annotation { "Feature Type Name" : "Feature", "Feature Type Description" : "" }
export const myFeature = defineFeature(function(context is Context, id is Id, definition is map)
    precondition{}
    {
        {
            var Q0;
            Q0=qCreatedBy(makeId("Front.planeOp"),FACE);
            var sketch = newSketch(context, id + "F0", { "sketchPlane" : qUnion([Q0])});
            skLineSegment(sketch, "E0", {"start": v(-75.47, 38.87) * mm, "end": v(-75.47, -34.46) * mm});
            skLineSegment(sketch, "E1.MirrorCS", {"start": v(75.47, 38.87) * mm, "end": v(75.47, -34.46) * mm});
            skLineSegment(sketch, "E2", {"start": v(-75.47, -34.46) * mm, "end": v(75.47, -34.46) * mm});
            skLineSegment(sketch, "E3", {"start": v(-75.47, 38.87) * mm, "end": v(75.47, 38.87) * mm});
            skText(sketch, "E4", { "text": "Rap Monster", "fontName": "OpenSans-Regular.ttf"});
            skText(sketch, "E5", { "text": "94", "fontName": "OpenSans-Regular.ttf"});
            const initialGuessF0  = {"E4": [-0.03494, 0.0229, 1, 0, 0.00846], "E5": [-0.03435, -0.02477, 1, 0, 0.04185]};
            skSetInitialGuess(sketch, initialGuessF0);
            skSolve(sketch);
        }
        {
            var Q0;
            Q0=makeQuery(id+"F0.imprint","IMPRINT",FACE,{"disambiguationData":[TD([[makeQuery(id+"F0.imprint","IMPRINT",EDGE,{"derivedFrom":sQuery(id+"F0.wireOp",EDGE,"E0")}),1.0]])]});
            extrude(context, id + "F1", {"entities" : qUnion([Q0]), "depth" : 3 * mm, "offsetDistance" : 25.4 * mm});
        }
        {
            var Q0;
            Q0=qCreatedBy(makeId("Front.planeOp"),FACE);
            var sketch = newSketch(context, id + "F2", { "sketchPlane" : qUnion([Q0])});
            skLineSegment(sketch, "E6.bottom", {"start": v(75.47, 38.9) * mm, "end": v(-75.55, 38.9) * mm});
            skLineSegment(sketch, "E6.top", {"start": v(75.47, -34.58) * mm, "end": v(-75.55, -34.58) * mm});
            skLineSegment(sketch, "E6.left", {"start": v(75.47, 38.9) * mm, "end": v(75.47, -34.58) * mm});
            skLineSegment(sketch, "E6.right", {"start": v(-75.55, 38.9) * mm, "end": v(-75.55, -34.58) * mm});
            skSolve(sketch);
        }
        {
            var Q0;
            Q0 = qSketchRegion(id + "F2", true);
            extrude(context, id + "F3", {"entities" : qUnion([Q0]), "operationType" : NewBodyOperationType.ADD, "oppositeDirection" : true, "depth" : 3 * mm, "offsetDistance" : 25.4 * mm});
        }
        {
            var Q0;
            Q0=makeQuery(id+"F0.imprint","IMPRINT",FACE,{"disambiguationData":[TD([[makeQuery(id+"F0.imprint","IMPRINT",EDGE,{"derivedFrom":sQuery(id+"F0.wireOp",EDGE,"E5.sketch_text.stroke-37")}),1.0]])]});
            var Q1;
            Q1=makeQuery(id+"F0.imprint","IMPRINT",FACE,{"disambiguationData":[TD([[makeQuery(id+"F0.imprint","IMPRINT",EDGE,{"derivedFrom":sQuery(id+"F0.wireOp",EDGE,"E5.sketch_text.stroke-16")}),1.0]])]});
            var Q2;
            Q2=makeQuery(id+"F0.imprint","IMPRINT",FACE,{"disambiguationData":[TD([[makeQuery(id+"F0.imprint","IMPRINT",EDGE,{"derivedFrom":sQuery(id+"F0.wireOp",EDGE,"E4.sketch_text.stroke-37")}),1.0]])]});
            var Q3;
            Q3=makeQuery(id+"F0.imprint","IMPRINT",FACE,{"disambiguationData":[TD([[makeQuery(id+"F0.imprint","IMPRINT",EDGE,{"derivedFrom":sQuery(id+"F0.wireOp",EDGE,"E4.sketch_text.stroke-11")}),1.0]])]});
            var Q4;
            Q4=makeQuery(id+"F0.imprint","IMPRINT",FACE,{"disambiguationData":[TD([[makeQuery(id+"F0.imprint","IMPRINT",EDGE,{"derivedFrom":sQuery(id+"F0.wireOp",EDGE,"E4.sketch_text.stroke-61")}),1.0]])]});
            var Q5;
            Q5=makeQuery(id+"F0.imprint","IMPRINT",FACE,{"disambiguationData":[TD([[makeQuery(id+"F0.imprint","IMPRINT",EDGE,{"derivedFrom":sQuery(id+"F0.wireOp",EDGE,"E4.sketch_text.stroke-97")}),1.0]])]});
            var Q6;
            Q6=makeQuery(id+"F0.imprint","IMPRINT",FACE,{"disambiguationData":[TD([[makeQuery(id+"F0.imprint","IMPRINT",EDGE,{"derivedFrom":sQuery(id+"F0.wireOp",EDGE,"E4.sketch_text.stroke-180")}),1.0]])]});
            extrude(context, id + "F4", {"entities" : qUnion([Q0, Q1, Q2, Q3, Q4, Q5, Q6]), "operationType" : NewBodyOperationType.ADD, "depth" : 3 * mm, "offsetDistance" : 25.4 * mm});
        }
        {
            var Q0;
            Q0=makeQuery(id+"F1.opExtrude","CAP_FACE",FACE,{"disambiguationData":[OSD([sQuery(id+"F0.wireOp",EDGE,"E0"),sQuery(id+"F0.wireOp",EDGE,"E1.MirrorCS"),sQuery(id+"F0.wireOp",EDGE,"E2"),sQuery(id+"F0.wireOp",EDGE,"E3"),sQuery(id+"F0.wireOp",EDGE,"E4.sketch_text.stroke-0"),sQuery(id+"F0.wireOp",EDGE,"E4.sketch_text.stroke-1"),sQuery(id+"F0.wireOp",EDGE,"E4.sketch_text.stroke-2"),sQuery(id+"F0.wireOp",EDGE,"E4.sketch_text.stroke-3"),sQuery(id+"F0.wireOp",EDGE,"E4.sketch_text.stroke-4"),sQuery(id+"F0.wireOp",EDGE,"E4.sketch_text.stroke-5"),sQuery(id+"F0.wireOp",EDGE,"E4.sketch_text.stroke-6"),sQuery(id+"F0.wireOp",EDGE,"E4.sketch_text.stroke-7"),sQuery(id+"F0.wireOp",EDGE,"E4.sketch_text.stroke-8"),sQuery(id+"F0.wireOp",EDGE,"E4.sketch_text.stroke-9"),sQuery(id+"F0.wireOp",EDGE,"E4.sketch_text.stroke-10"),sQuery(id+"F0.wireOp",EDGE,"E4.sketch_text.stroke-18"),sQuery(id+"F0.wireOp",EDGE,"E4.sketch_text.stroke-19"),sQuery(id+"F0.wireOp",EDGE,"E4.sketch_text.stroke-20"),sQuery(id+"F0.wireOp",EDGE,"E4.sketch_text.stroke-21"),sQuery(id+"F0.wireOp",EDGE,"E4.sketch_text.stroke-22"),sQuery(id+"F0.wireOp",EDGE,"E4.sketch_text.stroke-23"),sQuery(id+"F0.wireOp",EDGE,"E4.sketch_text.stroke-24"),sQuery(id+"F0.wireOp",EDGE,"E4.sketch_text.stroke-25"),sQuery(id+"F0.wireOp",EDGE,"E4.sketch_text.stroke-26"),sQuery(id+"F0.wireOp",EDGE,"E4.sketch_text.stroke-27"),sQuery(id+"F0.wireOp",EDGE,"E4.sketch_text.stroke-28"),sQuery(id+"F0.wireOp",EDGE,"E4.sketch_text.stroke-29"),sQuery(id+"F0.wireOp",EDGE,"E4.sketch_text.stroke-30"),sQuery(id+"F0.wireOp",EDGE,"E4.sketch_text.stroke-31"),sQuery(id+"F0.wireOp",EDGE,"E4.sketch_text.stroke-32"),sQuery(id+"F0.wireOp",EDGE,"E4.sketch_text.stroke-33"),sQuery(id+"F0.wireOp",EDGE,"E4.sketch_text.stroke-34"),sQuery(id+"F0.wireOp",EDGE,"E4.sketch_text.stroke-35"),sQuery(id+"F0.wireOp",EDGE,"E4.sketch_text.stroke-36"),sQuery(id+"F0.wireOp",EDGE,"E4.sketch_text.stroke-45"),sQuery(id+"F0.wireOp",EDGE,"E4.sketch_text.stroke-46"),sQuery(id+"F0.wireOp",EDGE,"E4.sketch_text.stroke-47"),sQuery(id+"F0.wireOp",EDGE,"E4.sketch_text.stroke-48"),sQuery(id+"F0.wireOp",EDGE,"E4.sketch_text.stroke-49"),sQuery(id+"F0.wireOp",EDGE,"E4.sketch_text.stroke-50"),sQuery(id+"F0.wireOp",EDGE,"E4.sketch_text.stroke-51"),sQuery(id+"F0.wireOp",EDGE,"E4.sketch_text.stroke-52"),sQuery(id+"F0.wireOp",EDGE,"E4.sketch_text.stroke-53"),sQuery(id+"F0.wireOp",EDGE,"E4.sketch_text.stroke-54"),sQuery(id+"F0.wireOp",EDGE,"E4.sketch_text.stroke-55"),sQuery(id+"F0.wireOp",EDGE,"E4.sketch_text.stroke-56"),sQuery(id+"F0.wireOp",EDGE,"E4.sketch_text.stroke-57"),sQuery(id+"F0.wireOp",EDGE,"E4.sketch_text.stroke-58"),sQuery(id+"F0.wireOp",EDGE,"E4.sketch_text.stroke-59"),sQuery(id+"F0.wireOp",EDGE,"E4.sketch_text.stroke-60"),sQuery(id+"F0.wireOp",EDGE,"E4.sketch_text.stroke-70"),sQuery(id+"F0.wireOp",EDGE,"E4.sketch_text.stroke-71"),sQuery(id+"F0.wireOp",EDGE,"E4.sketch_text.stroke-72"),sQuery(id+"F0.wireOp",EDGE,"E4.sketch_text.stroke-73"),sQuery(id+"F0.wireOp",EDGE,"E4.sketch_text.stroke-74"),sQuery(id+"F0.wireOp",EDGE,"E4.sketch_text.stroke-75"),sQuery(id+"F0.wireOp",EDGE,"E4.sketch_text.stroke-76"),sQuery(id+"F0.wireOp",EDGE,"E4.sketch_text.stroke-77"),sQuery(id+"F0.wireOp",EDGE,"E4.sketch_text.stroke-78"),sQuery(id+"F0.wireOp",EDGE,"E4.sketch_text.stroke-79"),sQuery(id+"F0.wireOp",EDGE,"E4.sketch_text.stroke-80"),sQuery(id+"F0.wireOp",EDGE,"E4.sketch_text.stroke-81"),sQuery(id+"F0.wireOp",EDGE,"E4.sketch_text.stroke-82"),sQuery(id+"F0.wireOp",EDGE,"E4.sketch_text.stroke-83"),sQuery(id+"F0.wireOp",EDGE,"E4.sketch_text.stroke-84"),sQuery(id+"F0.wireOp",EDGE,"E4.sketch_text.stroke-85"),sQuery(id+"F0.wireOp",EDGE,"E4.sketch_text.stroke-86"),sQuery(id+"F0.wireOp",EDGE,"E4.sketch_text.stroke-87"),sQuery(id+"F0.wireOp",EDGE,"E4.sketch_text.stroke-88"),sQuery(id+"F0.wireOp",EDGE,"E4.sketch_text.stroke-89"),sQuery(id+"F0.wireOp",EDGE,"E4.sketch_text.stroke-90"),sQuery(id+"F0.wireOp",EDGE,"E4.sketch_text.stroke-91"),sQuery(id+"F0.wireOp",EDGE,"E4.sketch_text.stroke-92"),sQuery(id+"F0.wireOp",EDGE,"E4.sketch_text.stroke-93"),sQuery(id+"F0.wireOp",EDGE,"E4.sketch_text.stroke-94"),sQuery(id+"F0.wireOp",EDGE,"E4.sketch_text.stroke-95"),sQuery(id+"F0.wireOp",EDGE,"E4.sketch_text.stroke-96"),sQuery(id+"F0.wireOp",EDGE,"E4.sketch_text.stroke-105"),sQuery(id+"F0.wireOp",EDGE,"E4.sketch_text.stroke-106"),sQuery(id+"F0.wireOp",EDGE,"E4.sketch_text.stroke-107"),sQuery(id+"F0.wireOp",EDGE,"E4.sketch_text.stroke-108"),sQuery(id+"F0.wireOp",EDGE,"E4.sketch_text.stroke-109"),sQuery(id+"F0.wireOp",EDGE,"E4.sketch_text.stroke-110"),sQuery(id+"F0.wireOp",EDGE,"E4.sketch_text.stroke-111"),sQuery(id+"F0.wireOp",EDGE,"E4.sketch_text.stroke-112"),sQuery(id+"F0.wireOp",EDGE,"E4.sketch_text.stroke-113"),sQuery(id+"F0.wireOp",EDGE,"E4.sketch_text.stroke-114"),sQuery(id+"F0.wireOp",EDGE,"E4.sketch_text.stroke-115"),sQuery(id+"F0.wireOp",EDGE,"E4.sketch_text.stroke-116"),sQuery(id+"F0.wireOp",EDGE,"E4.sketch_text.stroke-117"),sQuery(id+"F0.wireOp",EDGE,"E4.sketch_text.stroke-118"),sQuery(id+"F0.wireOp",EDGE,"E4.sketch_text.stroke-119"),sQuery(id+"F0.wireOp",EDGE,"E4.sketch_text.stroke-120"),sQuery(id+"F0.wireOp",EDGE,"E4.sketch_text.stroke-121"),sQuery(id+"F0.wireOp",EDGE,"E4.sketch_text.stroke-122"),sQuery(id+"F0.wireOp",EDGE,"E4.sketch_text.stroke-123"),sQuery(id+"F0.wireOp",EDGE,"E4.sketch_text.stroke-124"),sQuery(id+"F0.wireOp",EDGE,"E4.sketch_text.stroke-125"),sQuery(id+"F0.wireOp",EDGE,"E4.sketch_text.stroke-126"),sQuery(id+"F0.wireOp",EDGE,"E4.sketch_text.stroke-127"),sQuery(id+"F0.wireOp",EDGE,"E4.sketch_text.stroke-128"),sQuery(id+"F0.wireOp",EDGE,"E4.sketch_text.stroke-129"),sQuery(id+"F0.wireOp",EDGE,"E4.sketch_text.stroke-130"),sQuery(id+"F0.wireOp",EDGE,"E4.sketch_text.stroke-131"),sQuery(id+"F0.wireOp",EDGE,"E4.sketch_text.stroke-132"),sQuery(id+"F0.wireOp",EDGE,"E4.sketch_text.stroke-133"),sQuery(id+"F0.wireOp",EDGE,"E4.sketch_text.stroke-134"),sQuery(id+"F0.wireOp",EDGE,"E4.sketch_text.stroke-135"),sQuery(id+"F0.wireOp",EDGE,"E4.sketch_text.stroke-136"),sQuery(id+"F0.wireOp",EDGE,"E4.sketch_text.stroke-137"),sQuery(id+"F0.wireOp",EDGE,"E4.sketch_text.stroke-138"),sQuery(id+"F0.wireOp",EDGE,"E4.sketch_text.stroke-139"),sQuery(id+"F0.wireOp",EDGE,"E4.sketch_text.stroke-140"),sQuery(id+"F0.wireOp",EDGE,"E4.sketch_text.stroke-141"),sQuery(id+"F0.wireOp",EDGE,"E4.sketch_text.stroke-142"),sQuery(id+"F0.wireOp",EDGE,"E4.sketch_text.stroke-143"),sQuery(id+"F0.wireOp",EDGE,"E4.sketch_text.stroke-144"),sQuery(id+"F0.wireOp",EDGE,"E4.sketch_text.stroke-145"),sQuery(id+"F0.wireOp",EDGE,"E4.sketch_text.stroke-146"),sQuery(id+"F0.wireOp",EDGE,"E4.sketch_text.stroke-147"),sQuery(id+"F0.wireOp",EDGE,"E4.sketch_text.stroke-148"),sQuery(id+"F0.wireOp",EDGE,"E4.sketch_text.stroke-149"),sQuery(id+"F0.wireOp",EDGE,"E4.sketch_text.stroke-150"),sQuery(id+"F0.wireOp",EDGE,"E4.sketch_text.stroke-151"),sQuery(id+"F0.wireOp",EDGE,"E4.sketch_text.stroke-152"),sQuery(id+"F0.wireOp",EDGE,"E4.sketch_text.stroke-153"),sQuery(id+"F0.wireOp",EDGE,"E4.sketch_text.stroke-154"),sQuery(id+"F0.wireOp",EDGE,"E4.sketch_text.stroke-155"),sQuery(id+"F0.wireOp",EDGE,"E4.sketch_text.stroke-156"),sQuery(id+"F0.wireOp",EDGE,"E4.sketch_text.stroke-157"),sQuery(id+"F0.wireOp",EDGE,"E4.sketch_text.stroke-158"),sQuery(id+"F0.wireOp",EDGE,"E4.sketch_text.stroke-159"),sQuery(id+"F0.wireOp",EDGE,"E4.sketch_text.stroke-160"),sQuery(id+"F0.wireOp",EDGE,"E4.sketch_text.stroke-161"),sQuery(id+"F0.wireOp",EDGE,"E4.sketch_text.stroke-162"),sQuery(id+"F0.wireOp",EDGE,"E4.sketch_text.stroke-163"),sQuery(id+"F0.wireOp",EDGE,"E4.sketch_text.stroke-164"),sQuery(id+"F0.wireOp",EDGE,"E4.sketch_text.stroke-165"),sQuery(id+"F0.wireOp",EDGE,"E4.sketch_text.stroke-166"),sQuery(id+"F0.wireOp",EDGE,"E4.sketch_text.stroke-167"),sQuery(id+"F0.wireOp",EDGE,"E4.sketch_text.stroke-168"),sQuery(id+"F0.wireOp",EDGE,"E4.sketch_text.stroke-169"),sQuery(id+"F0.wireOp",EDGE,"E4.sketch_text.stroke-170"),sQuery(id+"F0.wireOp",EDGE,"E4.sketch_text.stroke-171"),sQuery(id+"F0.wireOp",EDGE,"E4.sketch_text.stroke-172"),sQuery(id+"F0.wireOp",EDGE,"E4.sketch_text.stroke-173"),sQuery(id+"F0.wireOp",EDGE,"E4.sketch_text.stroke-174"),sQuery(id+"F0.wireOp",EDGE,"E4.sketch_text.stroke-175"),sQuery(id+"F0.wireOp",EDGE,"E4.sketch_text.stroke-176"),sQuery(id+"F0.wireOp",EDGE,"E4.sketch_text.stroke-177"),sQuery(id+"F0.wireOp",EDGE,"E4.sketch_text.stroke-178"),sQuery(id+"F0.wireOp",EDGE,"E4.sketch_text.stroke-179"),sQuery(id+"F0.wireOp",EDGE,"E4.sketch_text.stroke-185"),sQuery(id+"F0.wireOp",EDGE,"E4.sketch_text.stroke-186"),sQuery(id+"F0.wireOp",EDGE,"E4.sketch_text.stroke-187"),sQuery(id+"F0.wireOp",EDGE,"E4.sketch_text.stroke-188"),sQuery(id+"F0.wireOp",EDGE,"E4.sketch_text.stroke-189"),sQuery(id+"F0.wireOp",EDGE,"E4.sketch_text.stroke-190"),sQuery(id+"F0.wireOp",EDGE,"E4.sketch_text.stroke-191"),sQuery(id+"F0.wireOp",EDGE,"E4.sketch_text.stroke-192"),sQuery(id+"F0.wireOp",EDGE,"E4.sketch_text.stroke-193"),sQuery(id+"F0.wireOp",EDGE,"E4.sketch_text.stroke-194"),sQuery(id+"F0.wireOp",EDGE,"E4.sketch_text.stroke-195"),sQuery(id+"F0.wireOp",EDGE,"E4.sketch_text.stroke-196"),sQuery(id+"F0.wireOp",EDGE,"E4.sketch_text.stroke-197"),sQuery(id+"F0.wireOp",EDGE,"E5.sketch_text.stroke-0"),sQuery(id+"F0.wireOp",EDGE,"E5.sketch_text.stroke-1"),sQuery(id+"F0.wireOp",EDGE,"E5.sketch_text.stroke-2"),sQuery(id+"F0.wireOp",EDGE,"E5.sketch_text.stroke-3"),sQuery(id+"F0.wireOp",EDGE,"E5.sketch_text.stroke-4"),sQuery(id+"F0.wireOp",EDGE,"E5.sketch_text.stroke-5"),sQuery(id+"F0.wireOp",EDGE,"E5.sketch_text.stroke-6"),sQuery(id+"F0.wireOp",EDGE,"E5.sketch_text.stroke-7"),sQuery(id+"F0.wireOp",EDGE,"E5.sketch_text.stroke-8"),sQuery(id+"F0.wireOp",EDGE,"E5.sketch_text.stroke-9"),sQuery(id+"F0.wireOp",EDGE,"E5.sketch_text.stroke-10"),sQuery(id+"F0.wireOp",EDGE,"E5.sketch_text.stroke-11"),sQuery(id+"F0.wireOp",EDGE,"E5.sketch_text.stroke-12"),sQuery(id+"F0.wireOp",EDGE,"E5.sketch_text.stroke-13"),sQuery(id+"F0.wireOp",EDGE,"E5.sketch_text.stroke-14"),sQuery(id+"F0.wireOp",EDGE,"E5.sketch_text.stroke-15"),sQuery(id+"F0.wireOp",EDGE,"E5.sketch_text.stroke-26"),sQuery(id+"F0.wireOp",EDGE,"E5.sketch_text.stroke-27"),sQuery(id+"F0.wireOp",EDGE,"E5.sketch_text.stroke-28"),sQuery(id+"F0.wireOp",EDGE,"E5.sketch_text.stroke-29"),sQuery(id+"F0.wireOp",EDGE,"E5.sketch_text.stroke-30"),sQuery(id+"F0.wireOp",EDGE,"E5.sketch_text.stroke-31"),sQuery(id+"F0.wireOp",EDGE,"E5.sketch_text.stroke-32"),sQuery(id+"F0.wireOp",EDGE,"E5.sketch_text.stroke-33"),sQuery(id+"F0.wireOp",EDGE,"E5.sketch_text.stroke-34"),sQuery(id+"F0.wireOp",EDGE,"E5.sketch_text.stroke-35"),sQuery(id+"F0.wireOp",EDGE,"E5.sketch_text.stroke-36")])],"isStart":false});
            var sketch = newSketch(context, id + "F5", { "sketchPlane" : qUnion([Q0])});
            skPoint(sketch, "E7", {"position": v(-70.4, 34.58) * mm});
            skSolve(sketch);
        }
        {
            var Q0;
            Q0=sQuery(id+"F5.wireOp",VERTEX,"E7");
            var Q1;
            Q1=makeQuery(id+"F1.opExtrude","SWEPT_BODY",BODY,{"disambiguationData":[OSD([sQuery(id+"F0.wireOp",EDGE,"E0"),sQuery(id+"F0.wireOp",EDGE,"E1.MirrorCS"),sQuery(id+"F0.wireOp",EDGE,"E2"),sQuery(id+"F0.wireOp",EDGE,"E3"),sQuery(id+"F0.wireOp",EDGE,"E4.sketch_text.stroke-0"),sQuery(id+"F0.wireOp",EDGE,"E4.sketch_text.stroke-1"),sQuery(id+"F0.wireOp",EDGE,"E4.sketch_text.stroke-2"),sQuery(id+"F0.wireOp",EDGE,"E4.sketch_text.stroke-3"),sQuery(id+"F0.wireOp",EDGE,"E4.sketch_text.stroke-4"),sQuery(id+"F0.wireOp",EDGE,"E4.sketch_text.stroke-5"),sQuery(id+"F0.wireOp",EDGE,"E4.sketch_text.stroke-6"),sQuery(id+"F0.wireOp",EDGE,"E4.sketch_text.stroke-7"),sQuery(id+"F0.wireOp",EDGE,"E4.sketch_text.stroke-8"),sQuery(id+"F0.wireOp",EDGE,"E4.sketch_text.stroke-9"),sQuery(id+"F0.wireOp",EDGE,"E4.sketch_text.stroke-10"),sQuery(id+"F0.wireOp",EDGE,"E4.sketch_text.stroke-18"),sQuery(id+"F0.wireOp",EDGE,"E4.sketch_text.stroke-19"),sQuery(id+"F0.wireOp",EDGE,"E4.sketch_text.stroke-20"),sQuery(id+"F0.wireOp",EDGE,"E4.sketch_text.stroke-21"),sQuery(id+"F0.wireOp",EDGE,"E4.sketch_text.stroke-22"),sQuery(id+"F0.wireOp",EDGE,"E4.sketch_text.stroke-23"),sQuery(id+"F0.wireOp",EDGE,"E4.sketch_text.stroke-24"),sQuery(id+"F0.wireOp",EDGE,"E4.sketch_text.stroke-25"),sQuery(id+"F0.wireOp",EDGE,"E4.sketch_text.stroke-26"),sQuery(id+"F0.wireOp",EDGE,"E4.sketch_text.stroke-27"),sQuery(id+"F0.wireOp",EDGE,"E4.sketch_text.stroke-28"),sQuery(id+"F0.wireOp",EDGE,"E4.sketch_text.stroke-29"),sQuery(id+"F0.wireOp",EDGE,"E4.sketch_text.stroke-30"),sQuery(id+"F0.wireOp",EDGE,"E4.sketch_text.stroke-31"),sQuery(id+"F0.wireOp",EDGE,"E4.sketch_text.stroke-32"),sQuery(id+"F0.wireOp",EDGE,"E4.sketch_text.stroke-33"),sQuery(id+"F0.wireOp",EDGE,"E4.sketch_text.stroke-34"),sQuery(id+"F0.wireOp",EDGE,"E4.sketch_text.stroke-35"),sQuery(id+"F0.wireOp",EDGE,"E4.sketch_text.stroke-36"),sQuery(id+"F0.wireOp",EDGE,"E4.sketch_text.stroke-45"),sQuery(id+"F0.wireOp",EDGE,"E4.sketch_text.stroke-46"),sQuery(id+"F0.wireOp",EDGE,"E4.sketch_text.stroke-47"),sQuery(id+"F0.wireOp",EDGE,"E4.sketch_text.stroke-48"),sQuery(id+"F0.wireOp",EDGE,"E4.sketch_text.stroke-49"),sQuery(id+"F0.wireOp",EDGE,"E4.sketch_text.stroke-50"),sQuery(id+"F0.wireOp",EDGE,"E4.sketch_text.stroke-51"),sQuery(id+"F0.wireOp",EDGE,"E4.sketch_text.stroke-52"),sQuery(id+"F0.wireOp",EDGE,"E4.sketch_text.stroke-53"),sQuery(id+"F0.wireOp",EDGE,"E4.sketch_text.stroke-54"),sQuery(id+"F0.wireOp",EDGE,"E4.sketch_text.stroke-55"),sQuery(id+"F0.wireOp",EDGE,"E4.sketch_text.stroke-56"),sQuery(id+"F0.wireOp",EDGE,"E4.sketch_text.stroke-57"),sQuery(id+"F0.wireOp",EDGE,"E4.sketch_text.stroke-58"),sQuery(id+"F0.wireOp",EDGE,"E4.sketch_text.stroke-59"),sQuery(id+"F0.wireOp",EDGE,"E4.sketch_text.stroke-60"),sQuery(id+"F0.wireOp",EDGE,"E4.sketch_text.stroke-70"),sQuery(id+"F0.wireOp",EDGE,"E4.sketch_text.stroke-71"),sQuery(id+"F0.wireOp",EDGE,"E4.sketch_text.stroke-72"),sQuery(id+"F0.wireOp",EDGE,"E4.sketch_text.stroke-73"),sQuery(id+"F0.wireOp",EDGE,"E4.sketch_text.stroke-74"),sQuery(id+"F0.wireOp",EDGE,"E4.sketch_text.stroke-75"),sQuery(id+"F0.wireOp",EDGE,"E4.sketch_text.stroke-76"),sQuery(id+"F0.wireOp",EDGE,"E4.sketch_text.stroke-77"),sQuery(id+"F0.wireOp",EDGE,"E4.sketch_text.stroke-78"),sQuery(id+"F0.wireOp",EDGE,"E4.sketch_text.stroke-79"),sQuery(id+"F0.wireOp",EDGE,"E4.sketch_text.stroke-80"),sQuery(id+"F0.wireOp",EDGE,"E4.sketch_text.stroke-81"),sQuery(id+"F0.wireOp",EDGE,"E4.sketch_text.stroke-82"),sQuery(id+"F0.wireOp",EDGE,"E4.sketch_text.stroke-83"),sQuery(id+"F0.wireOp",EDGE,"E4.sketch_text.stroke-84"),sQuery(id+"F0.wireOp",EDGE,"E4.sketch_text.stroke-85"),sQuery(id+"F0.wireOp",EDGE,"E4.sketch_text.stroke-86"),sQuery(id+"F0.wireOp",EDGE,"E4.sketch_text.stroke-87"),sQuery(id+"F0.wireOp",EDGE,"E4.sketch_text.stroke-88"),sQuery(id+"F0.wireOp",EDGE,"E4.sketch_text.stroke-89"),sQuery(id+"F0.wireOp",EDGE,"E4.sketch_text.stroke-90"),sQuery(id+"F0.wireOp",EDGE,"E4.sketch_text.stroke-91"),sQuery(id+"F0.wireOp",EDGE,"E4.sketch_text.stroke-92"),sQuery(id+"F0.wireOp",EDGE,"E4.sketch_text.stroke-93"),sQuery(id+"F0.wireOp",EDGE,"E4.sketch_text.stroke-94"),sQuery(id+"F0.wireOp",EDGE,"E4.sketch_text.stroke-95"),sQuery(id+"F0.wireOp",EDGE,"E4.sketch_text.stroke-96"),sQuery(id+"F0.wireOp",EDGE,"E4.sketch_text.stroke-105"),sQuery(id+"F0.wireOp",EDGE,"E4.sketch_text.stroke-106"),sQuery(id+"F0.wireOp",EDGE,"E4.sketch_text.stroke-107"),sQuery(id+"F0.wireOp",EDGE,"E4.sketch_text.stroke-108"),sQuery(id+"F0.wireOp",EDGE,"E4.sketch_text.stroke-109"),sQuery(id+"F0.wireOp",EDGE,"E4.sketch_text.stroke-110"),sQuery(id+"F0.wireOp",EDGE,"E4.sketch_text.stroke-111"),sQuery(id+"F0.wireOp",EDGE,"E4.sketch_text.stroke-112"),sQuery(id+"F0.wireOp",EDGE,"E4.sketch_text.stroke-113"),sQuery(id+"F0.wireOp",EDGE,"E4.sketch_text.stroke-114"),sQuery(id+"F0.wireOp",EDGE,"E4.sketch_text.stroke-115"),sQuery(id+"F0.wireOp",EDGE,"E4.sketch_text.stroke-116"),sQuery(id+"F0.wireOp",EDGE,"E4.sketch_text.stroke-117"),sQuery(id+"F0.wireOp",EDGE,"E4.sketch_text.stroke-118"),sQuery(id+"F0.wireOp",EDGE,"E4.sketch_text.stroke-119"),sQuery(id+"F0.wireOp",EDGE,"E4.sketch_text.stroke-120"),sQuery(id+"F0.wireOp",EDGE,"E4.sketch_text.stroke-121"),sQuery(id+"F0.wireOp",EDGE,"E4.sketch_text.stroke-122"),sQuery(id+"F0.wireOp",EDGE,"E4.sketch_text.stroke-123"),sQuery(id+"F0.wireOp",EDGE,"E4.sketch_text.stroke-124"),sQuery(id+"F0.wireOp",EDGE,"E4.sketch_text.stroke-125"),sQuery(id+"F0.wireOp",EDGE,"E4.sketch_text.stroke-126"),sQuery(id+"F0.wireOp",EDGE,"E4.sketch_text.stroke-127"),sQuery(id+"F0.wireOp",EDGE,"E4.sketch_text.stroke-128"),sQuery(id+"F0.wireOp",EDGE,"E4.sketch_text.stroke-129"),sQuery(id+"F0.wireOp",EDGE,"E4.sketch_text.stroke-130"),sQuery(id+"F0.wireOp",EDGE,"E4.sketch_text.stroke-131"),sQuery(id+"F0.wireOp",EDGE,"E4.sketch_text.stroke-132"),sQuery(id+"F0.wireOp",EDGE,"E4.sketch_text.stroke-133"),sQuery(id+"F0.wireOp",EDGE,"E4.sketch_text.stroke-134"),sQuery(id+"F0.wireOp",EDGE,"E4.sketch_text.stroke-135"),sQuery(id+"F0.wireOp",EDGE,"E4.sketch_text.stroke-136"),sQuery(id+"F0.wireOp",EDGE,"E4.sketch_text.stroke-137"),sQuery(id+"F0.wireOp",EDGE,"E4.sketch_text.stroke-138"),sQuery(id+"F0.wireOp",EDGE,"E4.sketch_text.stroke-139"),sQuery(id+"F0.wireOp",EDGE,"E4.sketch_text.stroke-140"),sQuery(id+"F0.wireOp",EDGE,"E4.sketch_text.stroke-141"),sQuery(id+"F0.wireOp",EDGE,"E4.sketch_text.stroke-142"),sQuery(id+"F0.wireOp",EDGE,"E4.sketch_text.stroke-143"),sQuery(id+"F0.wireOp",EDGE,"E4.sketch_text.stroke-144"),sQuery(id+"F0.wireOp",EDGE,"E4.sketch_text.stroke-145"),sQuery(id+"F0.wireOp",EDGE,"E4.sketch_text.stroke-146"),sQuery(id+"F0.wireOp",EDGE,"E4.sketch_text.stroke-147"),sQuery(id+"F0.wireOp",EDGE,"E4.sketch_text.stroke-148"),sQuery(id+"F0.wireOp",EDGE,"E4.sketch_text.stroke-149"),sQuery(id+"F0.wireOp",EDGE,"E4.sketch_text.stroke-150"),sQuery(id+"F0.wireOp",EDGE,"E4.sketch_text.stroke-151"),sQuery(id+"F0.wireOp",EDGE,"E4.sketch_text.stroke-152"),sQuery(id+"F0.wireOp",EDGE,"E4.sketch_text.stroke-153"),sQuery(id+"F0.wireOp",EDGE,"E4.sketch_text.stroke-154"),sQuery(id+"F0.wireOp",EDGE,"E4.sketch_text.stroke-155"),sQuery(id+"F0.wireOp",EDGE,"E4.sketch_text.stroke-156"),sQuery(id+"F0.wireOp",EDGE,"E4.sketch_text.stroke-157"),sQuery(id+"F0.wireOp",EDGE,"E4.sketch_text.stroke-158"),sQuery(id+"F0.wireOp",EDGE,"E4.sketch_text.stroke-159"),sQuery(id+"F0.wireOp",EDGE,"E4.sketch_text.stroke-160"),sQuery(id+"F0.wireOp",EDGE,"E4.sketch_text.stroke-161"),sQuery(id+"F0.wireOp",EDGE,"E4.sketch_text.stroke-162"),sQuery(id+"F0.wireOp",EDGE,"E4.sketch_text.stroke-163"),sQuery(id+"F0.wireOp",EDGE,"E4.sketch_text.stroke-164"),sQuery(id+"F0.wireOp",EDGE,"E4.sketch_text.stroke-165"),sQuery(id+"F0.wireOp",EDGE,"E4.sketch_text.stroke-166"),sQuery(id+"F0.wireOp",EDGE,"E4.sketch_text.stroke-167"),sQuery(id+"F0.wireOp",EDGE,"E4.sketch_text.stroke-168"),sQuery(id+"F0.wireOp",EDGE,"E4.sketch_text.stroke-169"),sQuery(id+"F0.wireOp",EDGE,"E4.sketch_text.stroke-170"),sQuery(id+"F0.wireOp",EDGE,"E4.sketch_text.stroke-171"),sQuery(id+"F0.wireOp",EDGE,"E4.sketch_text.stroke-172"),sQuery(id+"F0.wireOp",EDGE,"E4.sketch_text.stroke-173"),sQuery(id+"F0.wireOp",EDGE,"E4.sketch_text.stroke-174"),sQuery(id+"F0.wireOp",EDGE,"E4.sketch_text.stroke-175"),sQuery(id+"F0.wireOp",EDGE,"E4.sketch_text.stroke-176"),sQuery(id+"F0.wireOp",EDGE,"E4.sketch_text.stroke-177"),sQuery(id+"F0.wireOp",EDGE,"E4.sketch_text.stroke-178"),sQuery(id+"F0.wireOp",EDGE,"E4.sketch_text.stroke-179"),sQuery(id+"F0.wireOp",EDGE,"E4.sketch_text.stroke-185"),sQuery(id+"F0.wireOp",EDGE,"E4.sketch_text.stroke-186"),sQuery(id+"F0.wireOp",EDGE,"E4.sketch_text.stroke-187"),sQuery(id+"F0.wireOp",EDGE,"E4.sketch_text.stroke-188"),sQuery(id+"F0.wireOp",EDGE,"E4.sketch_text.stroke-189"),sQuery(id+"F0.wireOp",EDGE,"E4.sketch_text.stroke-190"),sQuery(id+"F0.wireOp",EDGE,"E4.sketch_text.stroke-191"),sQuery(id+"F0.wireOp",EDGE,"E4.sketch_text.stroke-192"),sQuery(id+"F0.wireOp",EDGE,"E4.sketch_text.stroke-193"),sQuery(id+"F0.wireOp",EDGE,"E4.sketch_text.stroke-194"),sQuery(id+"F0.wireOp",EDGE,"E4.sketch_text.stroke-195"),sQuery(id+"F0.wireOp",EDGE,"E4.sketch_text.stroke-196"),sQuery(id+"F0.wireOp",EDGE,"E4.sketch_text.stroke-197"),sQuery(id+"F0.wireOp",EDGE,"E5.sketch_text.stroke-0"),sQuery(id+"F0.wireOp",EDGE,"E5.sketch_text.stroke-1"),sQuery(id+"F0.wireOp",EDGE,"E5.sketch_text.stroke-2"),sQuery(id+"F0.wireOp",EDGE,"E5.sketch_text.stroke-3"),sQuery(id+"F0.wireOp",EDGE,"E5.sketch_text.stroke-4"),sQuery(id+"F0.wireOp",EDGE,"E5.sketch_text.stroke-5"),sQuery(id+"F0.wireOp",EDGE,"E5.sketch_text.stroke-6"),sQuery(id+"F0.wireOp",EDGE,"E5.sketch_text.stroke-7"),sQuery(id+"F0.wireOp",EDGE,"E5.sketch_text.stroke-8"),sQuery(id+"F0.wireOp",EDGE,"E5.sketch_text.stroke-9"),sQuery(id+"F0.wireOp",EDGE,"E5.sketch_text.stroke-10"),sQuery(id+"F0.wireOp",EDGE,"E5.sketch_text.stroke-11"),sQuery(id+"F0.wireOp",EDGE,"E5.sketch_text.stroke-12"),sQuery(id+"F0.wireOp",EDGE,"E5.sketch_text.stroke-13"),sQuery(id+"F0.wireOp",EDGE,"E5.sketch_text.stroke-14"),sQuery(id+"F0.wireOp",EDGE,"E5.sketch_text.stroke-15"),sQuery(id+"F0.wireOp",EDGE,"E5.sketch_text.stroke-26"),sQuery(id+"F0.wireOp",EDGE,"E5.sketch_text.stroke-27"),sQuery(id+"F0.wireOp",EDGE,"E5.sketch_text.stroke-28"),sQuery(id+"F0.wireOp",EDGE,"E5.sketch_text.stroke-29"),sQuery(id+"F0.wireOp",EDGE,"E5.sketch_text.stroke-30"),sQuery(id+"F0.wireOp",EDGE,"E5.sketch_text.stroke-31"),sQuery(id+"F0.wireOp",EDGE,"E5.sketch_text.stroke-32"),sQuery(id+"F0.wireOp",EDGE,"E5.sketch_text.stroke-33"),sQuery(id+"F0.wireOp",EDGE,"E5.sketch_text.stroke-34"),sQuery(id+"F0.wireOp",EDGE,"E5.sketch_text.stroke-35"),sQuery(id+"F0.wireOp",EDGE,"E5.sketch_text.stroke-36")])]});
            hole(context, id + "F6", {"style" : HoleStyle.SIMPLE, "endStyle" : HoleEndStyle.BLIND, "holeDiameter" : 6.35 * mm, "majorDiameter" : 6.35 * mm, "holeDepth" : 6 * mm, "isTappedThrough" : true, "tappedDepth" : 12.7 * mm, "tapClearance" : 3, "locations" : qUnion([Q0]), "scope" : qUnion([Q1])});
        }
    });